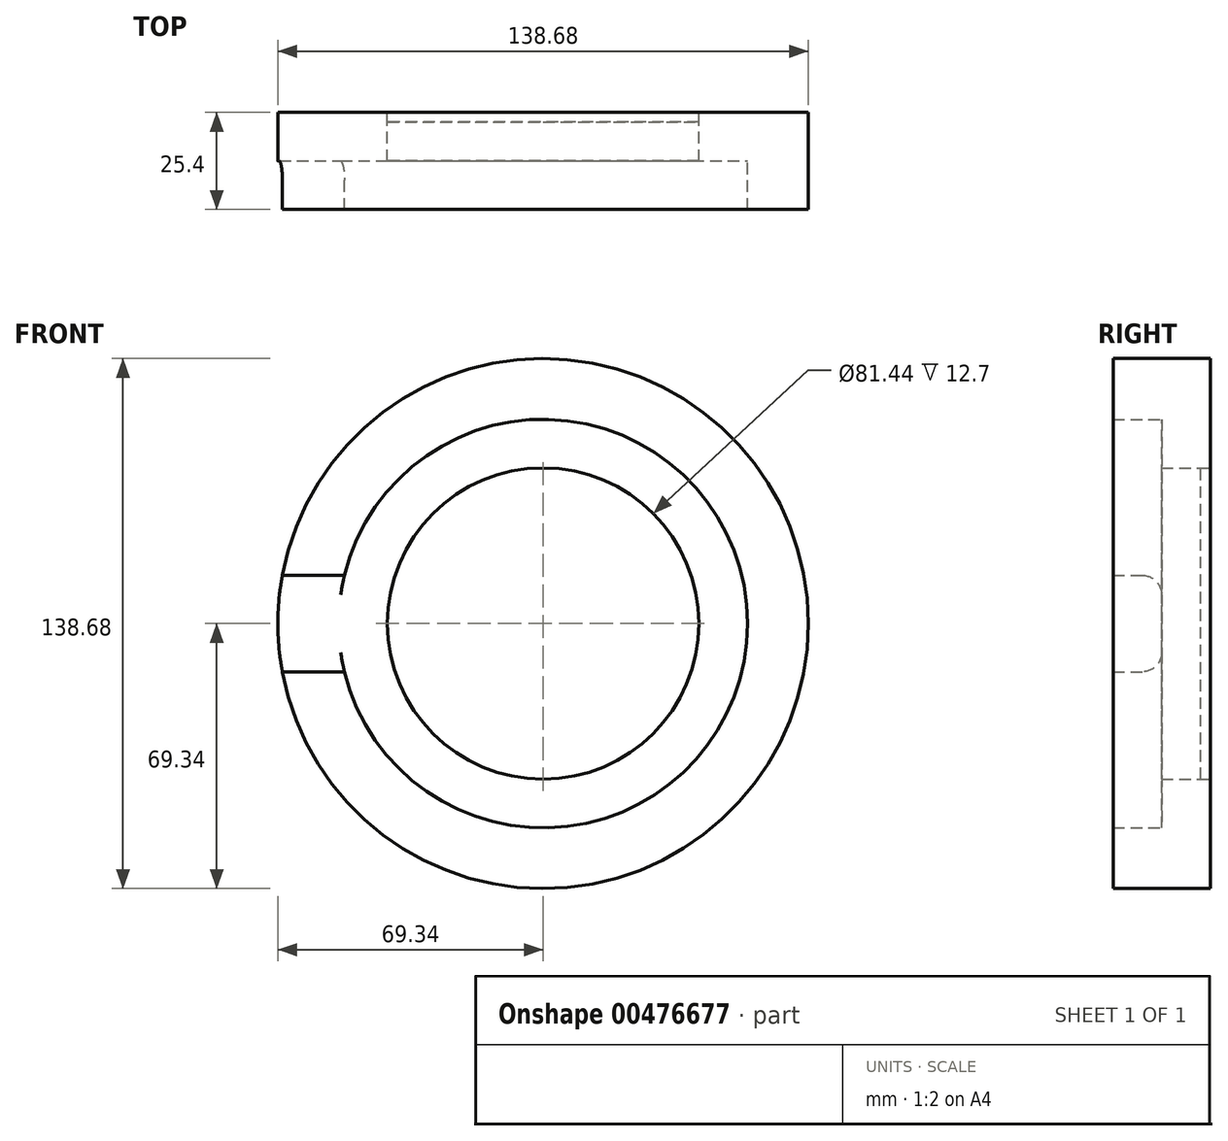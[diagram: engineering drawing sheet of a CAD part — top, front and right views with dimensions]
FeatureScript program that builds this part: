
annotation { "Feature Type Name" : "Feature", "Feature Type Description" : "" }
export const myFeature = defineFeature(function(context is Context, id is Id, definition is map)
    precondition{}
    {
        {
            var Q0;
            Q0=qCreatedBy(makeId("Front.planeOp"),FACE);
            var sketch = newSketch(context, id + "F0", { "sketchPlane" : qUnion([Q0])});
            skCircle(sketch, "E0", {"center": v(0, 0) * mm, "radius": 53.45 * mm});
            skCircle(sketch, "E1", {"center": v(0, 0) * mm, "radius": 40.72 * mm});
            skCircle(sketch, "E2", {"center": v(0, 0) * mm, "radius": 69.34 * mm});
            skSolve(sketch);
        }
        {
            var Q0;
            Q0=makeQuery(id+"F0.imprint","IMPRINT",FACE,{"disambiguationData":[TD([[makeQuery(id+"F0.imprint","IMPRINT",EDGE,{"derivedFrom":sQuery(id+"F0.wireOp",EDGE,"E1")}),1.0]])]});
            extrude(context, id + "F1", {"entities" : qUnion([Q0]), "depth" : 2.54 * mm});
        }
        {
            var Q0;
            Q0=makeQuery(id+"F0.imprint","IMPRINT",FACE,{"disambiguationData":[TD([[makeQuery(id+"F0.imprint","IMPRINT",EDGE,{"derivedFrom":sQuery(id+"F0.wireOp",EDGE,"E0")}),1.0]])]});
            extrude(context, id + "F2", {"entities" : qUnion([Q0]), "depth" : 12.7 * mm});
        }
        {
            var Q0;
            Q0=makeQuery(id+"F0.imprint","IMPRINT",FACE,{"disambiguationData":[TD([[makeQuery(id+"F0.imprint","IMPRINT",EDGE,{"derivedFrom":sQuery(id+"F0.wireOp",EDGE,"E0")}),-1.0]])]});
            extrude(context, id + "F3", {"entities" : qUnion([Q0]), "operationType" : NewBodyOperationType.ADD, "depth" : 25.4 * mm});
        }
        {
            var Q0;
            Q0=makeQuery(id+"F3.opExtrude","CAP_FACE",FACE,{"disambiguationData":[OSD([sQuery(id+"F0.wireOp",EDGE,"E0"),sQuery(id+"F0.wireOp",EDGE,"E2")])],"isStart":false});
            var sketch = newSketch(context, id + "F4", { "sketchPlane" : qUnion([Q0])});
            skLineSegment(sketch, "E3.bottom", {"start": v(-74.6, 12.63) * mm, "end": v(-51.1, 12.63) * mm});
            skLineSegment(sketch, "E3.top", {"start": v(-74.6, -12.63) * mm, "end": v(-51.1, -12.63) * mm});
            skLineSegment(sketch, "E3.left", {"start": v(-74.6, 12.63) * mm, "end": v(-74.6, -12.63) * mm});
            skLineSegment(sketch, "E3.right", {"start": v(-51.1, 12.63) * mm, "end": v(-51.1, -12.63) * mm});
            skPoint(sketch, "E3.middle", {"position": v(-62.85, 0) * mm});
            skSolve(sketch);
        }
        {
            var Q0;
            Q0 = qSketchRegion(id + "F4", true);
            extrude(context, id + "F5", {"entities" : qUnion([Q0]), "operationType" : NewBodyOperationType.REMOVE, "oppositeDirection" : true, "depth" : 12.7 * mm});
        }
        {
            var Q0;
            Q0=makeQuery(id+"F5.boolean.opBoolean","COPY",EDGE,{"derivedFrom":makeQuery(id+"F5.opExtrude","CAP_EDGE",EDGE,{"disambiguationData":[OSD([sQuery(id+"F4.wireOp",EDGE,"E3.bottom")])],"isStart":false})});
            var Q1;
            Q1=makeQuery(id+"F5.boolean.opBoolean","COPY",EDGE,{"derivedFrom":makeQuery(id+"F5.opExtrude","CAP_EDGE",EDGE,{"disambiguationData":[OSD([sQuery(id+"F4.wireOp",EDGE,"E3.top")])],"isStart":false})});
            var Q2;
            Q2=makeQuery(id+"F5.boolean.opBoolean","COPY",EDGE,{"derivedFrom":makeQuery(id+"F5.opExtrude","CAP_EDGE",EDGE,{"disambiguationData":[OSD([sQuery(id+"F4.wireOp",EDGE,"E3.top")])],"isStart":true})});
            var Q3;
            Q3=makeQuery(id+"F5.boolean.opBoolean","COPY",EDGE,{"derivedFrom":makeQuery(id+"F5.opExtrude","CAP_EDGE",EDGE,{"disambiguationData":[OSD([sQuery(id+"F4.wireOp",EDGE,"E3.bottom")])],"isStart":true})});
            fillet(context, id + "F6", {"entities" : qUnion([Q0, Q1, Q2, Q3]), "radius" : 5.08 * mm, "tangentPropagation" : true, "allowEdgeOverflow" : false});
        }
    });
